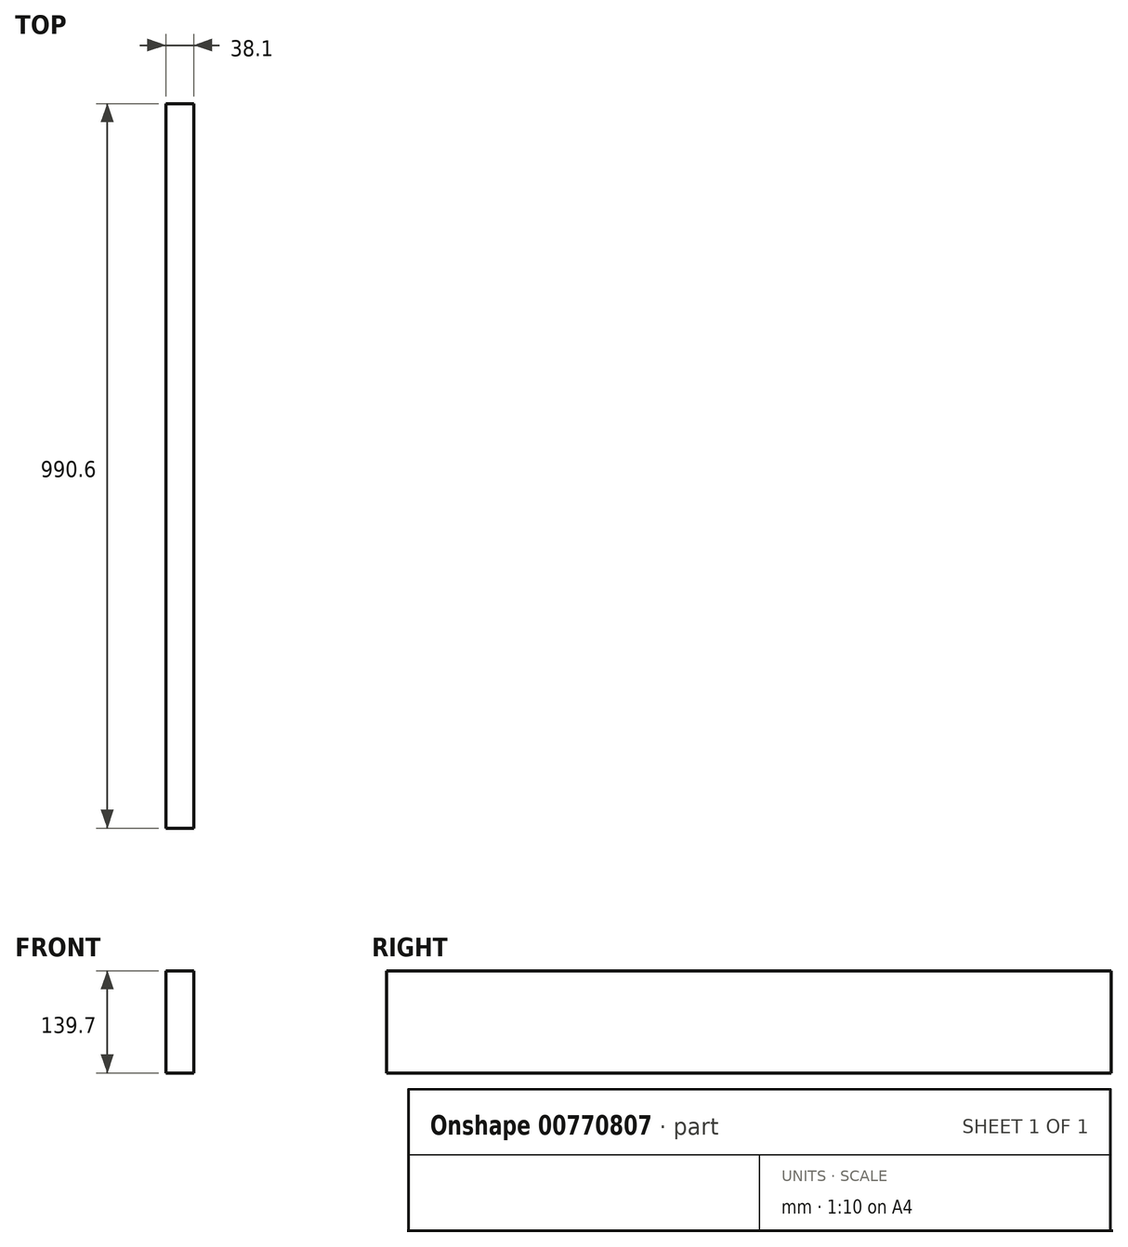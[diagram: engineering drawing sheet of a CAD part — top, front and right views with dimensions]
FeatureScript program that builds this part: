
annotation { "Feature Type Name" : "Feature", "Feature Type Description" : "" }
export const myFeature = defineFeature(function(context is Context, id is Id, definition is map)
    precondition{}
    {
        {
            var Q0;
            Q0=qCreatedBy(makeId("Front.planeOp"),FACE);
            var sketch = newSketch(context, id + "F0", { "sketchPlane" : qUnion([Q0])});
            skLineSegment(sketch, "E0.bottom", {"start": v(0, 0) * mm, "end": v(38.1, 0) * mm});
            skLineSegment(sketch, "E0.top", {"start": v(0, 139.7) * mm, "end": v(38.1, 139.7) * mm});
            skLineSegment(sketch, "E0.left", {"start": v(0, 0) * mm, "end": v(0, 139.7) * mm});
            skLineSegment(sketch, "E0.right", {"start": v(38.1, 0) * mm, "end": v(38.1, 139.7) * mm});
            skSolve(sketch);
        }
        {
            var Q0;
            Q0=makeQuery(id+"F0.imprint","IMPRINT",FACE,{"disambiguationData":[TD([[makeQuery(id+"F0.imprint","IMPRINT",EDGE,{"derivedFrom":sQuery(id+"F0.wireOp",EDGE,"E0.bottom")}),1.0]])]});
            extrude(context, id + "F1", {"entities" : qUnion([Q0]), "depth" : 990.6 * mm, "offsetDistance" : 25.4 * mm});
        }
    });
